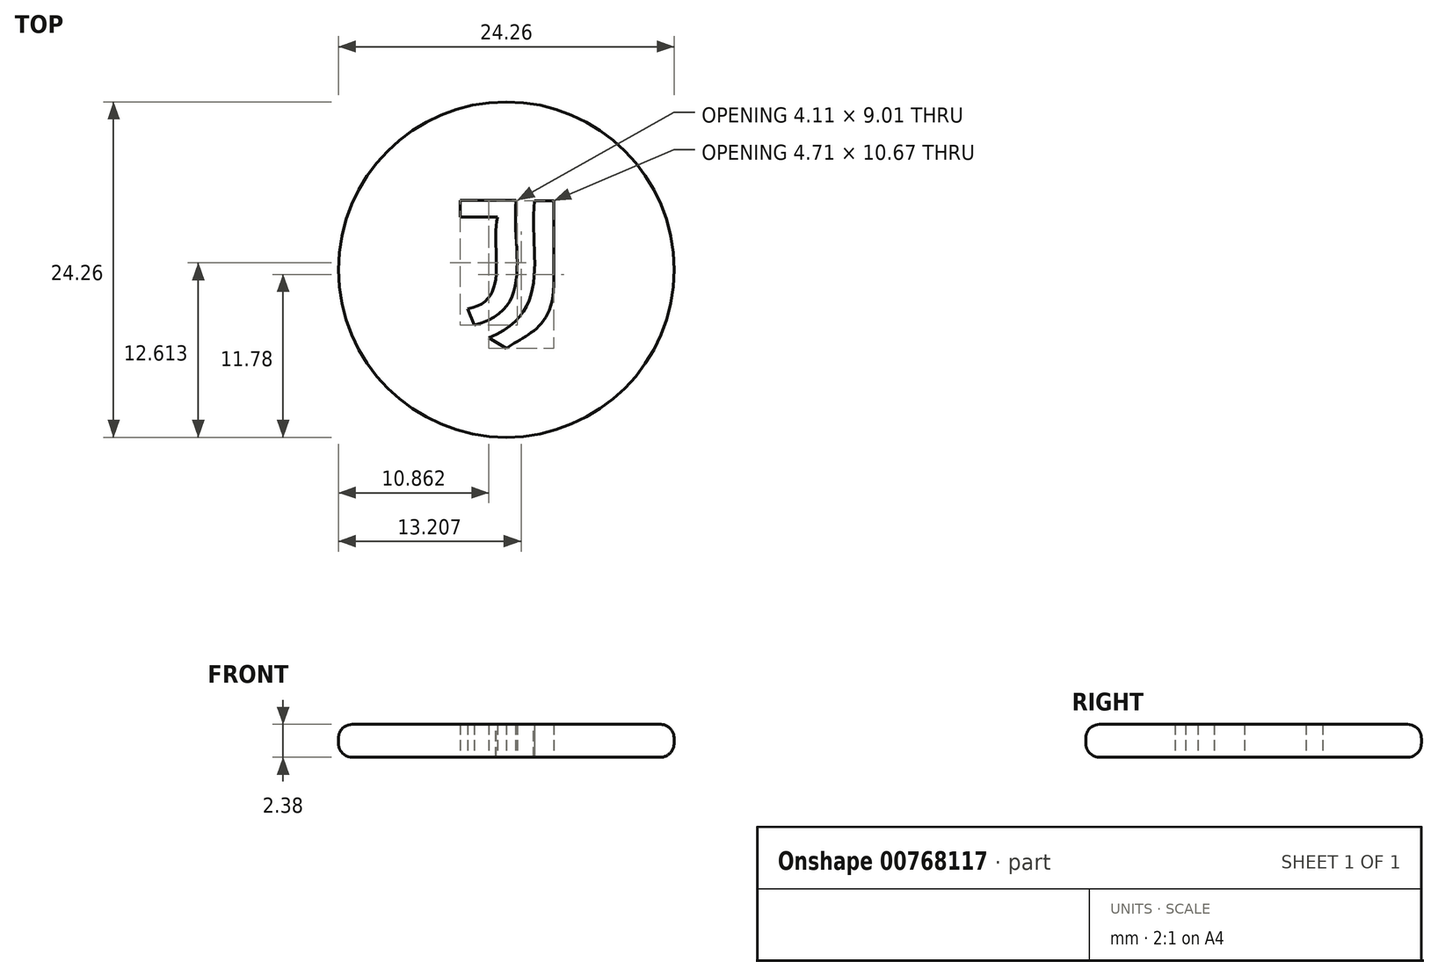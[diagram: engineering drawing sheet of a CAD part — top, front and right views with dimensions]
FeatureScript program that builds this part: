
annotation { "Feature Type Name" : "Feature", "Feature Type Description" : "" }
export const myFeature = defineFeature(function(context is Context, id is Id, definition is map)
    precondition{}
    {
        {
            var Q0;
            Q0=qCreatedBy(makeId("Top.planeOp"),FACE);
            var sketch = newSketch(context, id + "F0", { "sketchPlane" : qUnion([Q0])});
            skCircle(sketch, "E0", {"center": v(0, 0) * mm, "radius": 12.12 * mm});
            skLineSegment(sketch, "E1", {"start": v(-3.32, 4.99) * mm, "end": v(-3.32, 3.78) * mm});
            skLineSegment(sketch, "E2", {"start": v(-3.32, 3.78) * mm, "end": v(-0.64, 3.78) * mm});
            skLineSegment(sketch, "E3", {"start": v(-3.32, 4.99) * mm, "end": v(0.7, 4.99) * mm});
            skLineSegment(sketch, "E4", {"start": v(2.04, 4.98) * mm, "end": v(3.43, 4.98) * mm});
            skFitSpline(sketch, "E5", {"points": [v(0.7, 4.99) * mm, v(-2.33, -4.02) * mm], "startDerivative": vector(-0.9, -11.85) * mm, "endDerivative": vector(-13.35, -3.44) * mm});
            skFitSpline(sketch, "E6", {"points": [v(-0.64, 3.78) * mm, v(-2.8, -2.83) * mm], "startDerivative": vector(-1.6, -6.9) * mm, "endDerivative": vector(-9.56, -1.52) * mm});
            skLineSegment(sketch, "E7", {"start": v(-2.8, -2.83) * mm, "end": v(-2.33, -4.02) * mm});
            skFitSpline(sketch, "E8", {"points": [v(2.04, 4.98) * mm, v(-1.28, -4.92) * mm], "startDerivative": vector(-1.2, -11.7) * mm, "endDerivative": vector(-14.14, -5.7) * mm});
            skLineSegment(sketch, "E9", {"start": v(3.43, 4.98) * mm, "end": v(3.43, -0.67) * mm});
            skFitSpline(sketch, "E10", {"points": [v(3.43, -0.67) * mm, v(0, -5.68) * mm], "startDerivative": vector(0.38, -10.88) * mm, "endDerivative": vector(-4.12, -2.96) * mm});
            skLineSegment(sketch, "E11", {"start": v(-1.28, -4.92) * mm, "end": v(0, -5.68) * mm});
            skSolve(sketch);
        }
        {
            var Q0;
            Q0=makeQuery(id+"F0.imprint","IMPRINT",FACE,{"disambiguationData":[TD([[makeQuery(id+"F0.imprint","IMPRINT",EDGE,{"derivedFrom":sQuery(id+"F0.wireOp",EDGE,"E0")}),1.0]])]});
            extrude(context, id + "F1", {"entities" : qUnion([Q0]), "depth" : 2.38 * mm, "offsetDistance" : 25 * mm});
        }
        {
            var Q0;
            Q0=makeQuery(id+"F1.opExtrude","CAP_EDGE",EDGE,{"disambiguationData":[OSD([sQuery(id+"F0.wireOp",EDGE,"E0")])],"isStart":false});
            var Q1;
            Q1=makeQuery(id+"F1.opExtrude","CAP_EDGE",EDGE,{"disambiguationData":[OSD([sQuery(id+"F0.wireOp",EDGE,"E0")])],"isStart":true});
            fillet(context, id + "F2", {"entities" : qUnion([Q0, Q1]), "radius" : 1 * mm, "tangentPropagation" : true, "allowEdgeOverflow" : false});
        }
    });
